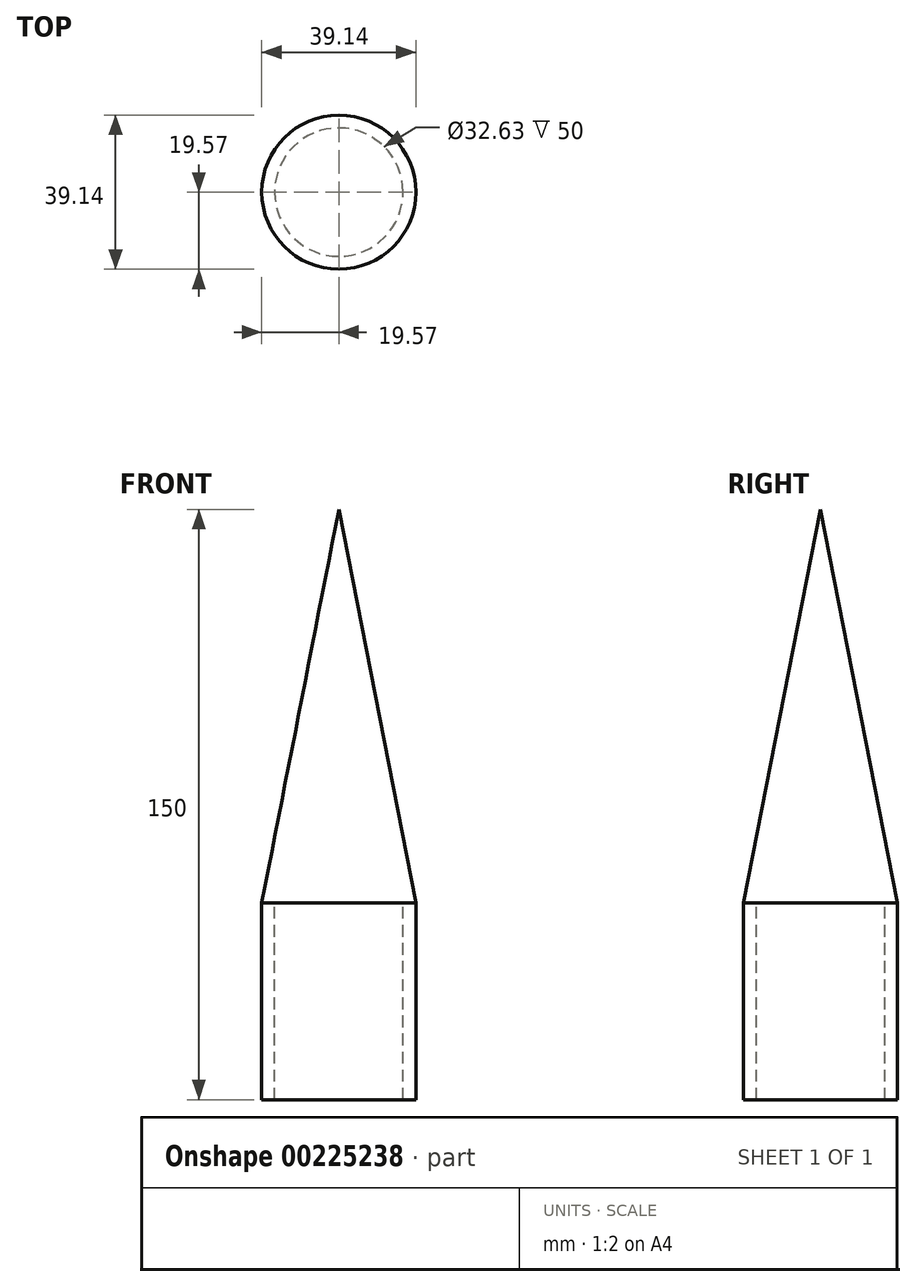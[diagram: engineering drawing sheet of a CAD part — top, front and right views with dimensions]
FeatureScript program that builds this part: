
annotation { "Feature Type Name" : "Feature", "Feature Type Description" : "" }
export const myFeature = defineFeature(function(context is Context, id is Id, definition is map)
    precondition{}
    {
        {
            var Q0;
            Q0=qCreatedBy(makeId("Front.planeOp"),FACE);
            var sketch = newSketch(context, id + "F0", { "sketchPlane" : qUnion([Q0])});
            skLineSegment(sketch, "E0", {"start": v(0, 0) * mm, "end": v(0, 100) * mm});
            skLineSegment(sketch, "E1", {"start": v(0, 100) * mm, "end": v(19.57, 0) * mm});
            skLineSegment(sketch, "E2", {"start": v(19.57, 0) * mm, "end": v(0, 0) * mm});
            skSolve(sketch);
        }
        {
            var Q0;
            Q0=makeQuery(id+"F0.imprint","IMPRINT",FACE,{"disambiguationData":[TD([[makeQuery(id+"F0.imprint","IMPRINT",EDGE,{"derivedFrom":sQuery(id+"F0.wireOp",EDGE,"E0")}),-1.0]])]});
            var Q1;
            Q1=sQuery(id+"F0.wireOp",EDGE,"E0");
            revolve(context, id + "F1", {"entities" : qUnion([Q0]), "axis" : qUnion([Q1]), "revolveType" : RevolveType.FULL});
        }
        {
            var Q0;
            Q0=makeQuery(id+"F1.opRevolve","SWEPT_FACE",FACE,{"disambiguationData":[OSD([sQuery(id+"F0.wireOp",EDGE,"E2")])]});
            var sketch = newSketch(context, id + "F2", { "sketchPlane" : qUnion([Q0])});
            skCircle(sketch, "E3", {"center": v(0, 0) * mm, "radius": 19.64 * mm});
            skCircle(sketch, "E4", {"center": v(0, 0) * mm, "radius": 16.32 * mm});
            skSolve(sketch);
        }
        {
            var Q0;
            Q0=makeQuery(id+"F2.imprint","IMPRINT",FACE,{"disambiguationData":[TD([[makeQuery(id+"F2.imprint","IMPRINT",EDGE,{"derivedFrom":sQuery(id+"F2.wireOp",EDGE,"E4")}),-1.0]])]});
            extrude(context, id + "F3", {"entities" : qUnion([Q0]), "operationType" : NewBodyOperationType.ADD, "depth" : 50 * mm});
        }
    });
